# Revit family: M_Ryterna_TLP VL
name_source: partatom
category: Doors
revit_build: Autodesk Revit 2018 (Build: 20190510_1515(x64)
units: mm (PartAtom-declared; Revit-internal decimal feet)

## family parameters
Always vertical = Yes
Cut with Voids When Loaded = No
Host = Wall
OmniClass Number = 23.30.10.00
OmniClass Title = Doors
Room Calculation Point = No
Shared = No

## types (1)
- TLP VL H3000W3000
    Beam H = 100 mm  [stored 0.328084 ft]
    Beam Material = Steel, Galvanized
    Bottom Gasket Material = Gasket Rubber, Black
    Clearance Zone = Yes
    Door Bottom Offset = 30 mm  [stored 0.0984252 ft]
    Door Height = 2980 mm
    Door Inset = 15 mm  [stored 0.0492126 ft]
    Door Type Color Material = M_Garage Door : RAL 9016/RAL 9002
    F = 50 mm  [stored 0.164042 ft]
    Guide Track Material = Steel, Galvanized
    Height = 3000 mm  [stored 9.84252 ft]
    Height_True = 3000 mm  [stored 9.84252 ft]
    Horizontal L Track Material = Steel, Galvanized
    Lifting Assembly Angle = 90.00°
    Lifting Assembly Horizontal Shift = 0 mm  [stored 0 ft]
    Lifting Type A = M_Lifting Assembly_VL : 1
    Lifting Type B = M_Lifting Assembly_VL : 2
    Lower Mounted Shaft = No
    Lower Mounted Shaft Clearance Zone = No
    Lower Mounted Shaft_True = No
    Manufacturer = UAB “RYTERNA GROUP”
    PO Host Position = 200 mm  [stored 0.656168 ft]
    Power Operator Position = , : None
    Power Operator Position Left = , : Right
    Power Operator Position Right = , : Left
    Pulley Material = Steel, Galvanized
    Reel Material = Steel, Galvanized
    Regular Clearance Zone = Yes
    Rod Material = Steel, Galvanized
    Roller Holder Material = Steel, Galvanized
    Rough Height = 3010 mm  [stored 9.87533 ft]
    Rough Width = 3040 mm  [stored 9.97375 ft]
    Spring Holder Material = Steel, Galvanized
    Spring Material = Steel, Galvanized
    Thickness = 40 mm  [stored 0.131234 ft]
    Top Gasket Material = Gasket Rubber, Black
    Triangle Connection Material = Steel, Galvanized
    Triangle Mounting Plate Material = Steel, Galvanized
    URL = https://www.ryterna.eu
    Vertical L Profile Material = Steel, Galvanized
    Wall Closure = By host
    Warning Message = No
    Width = 3000 mm  [stored 9.84252 ft]
    Width for Operator = 3000 mm  [stored 9.84252 ft]
    Width_True = 3000 mm  [stored 9.84252 ft]
    Zone Cut Inset = 0 mm  [stored 0 ft]
    Zone Left Lower PO Thickness = 260 mm  [stored 0.853018 ft]
    Zone Left Upper PO Thickness = -1650 mm  [stored -5.41339 ft]
    Zone Right Lower PO Thickness = 260 mm  [stored 0.853018 ft]
    Zone Right Upper PO Thickness = 1650 mm  [stored 5.41339 ft]
    Zone Sloped Thickness = 83 mm
    Zone Vertical Thickness = 155 mm

note: [stored X ft] marks values corroborated as IEEE doubles in the binary element streams (Revit-internal decimal feet)

## geometry (parser evidence)
native form markers: Blend x8, Extrusion x4, Sweep x63
no freeform markers — native parametric forms only
